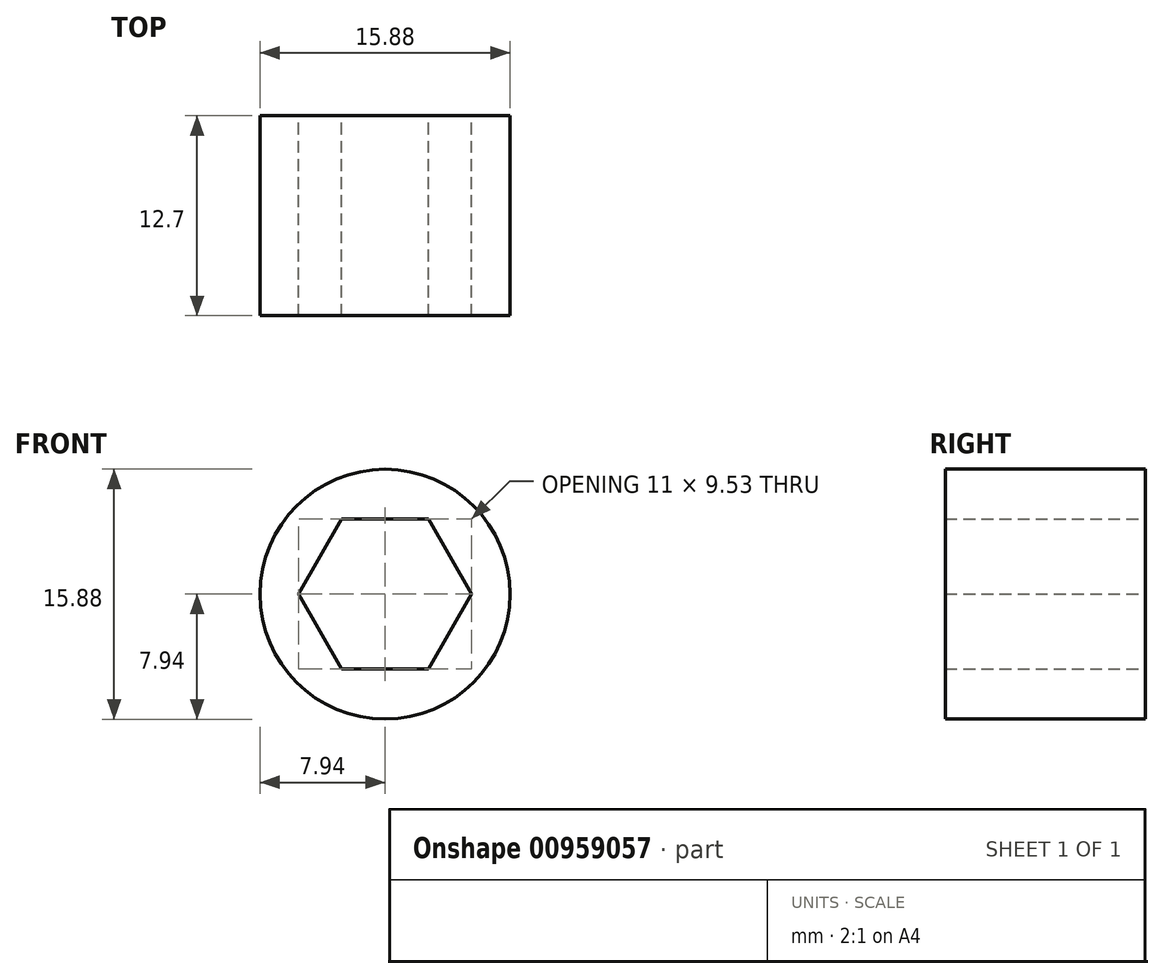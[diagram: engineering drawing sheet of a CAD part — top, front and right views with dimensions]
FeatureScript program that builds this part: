
annotation { "Feature Type Name" : "Feature", "Feature Type Description" : "" }
export const myFeature = defineFeature(function(context is Context, id is Id, definition is map)
    precondition{}
    {
        {
            var Q0;
            Q0=qCreatedBy(makeId("Front.planeOp"),FACE);
            var sketch = newSketch(context, id + "F0", { "sketchPlane" : qUnion([Q0])});
            skCircle(sketch, "E0", {"center": v(0, 0) * mm, "radius": 7.94 * mm});
            skCircle(sketch, "E1.cCircle", {"center": v(0, 0) * mm, "radius": 4.76 * mm, "construction": true});
            skLineSegment(sketch, "E1.0", {"start": v(-2.75, 4.76) * mm, "end": v(2.75, 4.76) * mm});
            skLineSegment(sketch, "E1.1", {"start": v(2.75, 4.76) * mm, "end": v(5.5, 0) * mm});
            skLineSegment(sketch, "E1.2", {"start": v(5.5, 0) * mm, "end": v(2.75, -4.76) * mm});
            skLineSegment(sketch, "E1.3", {"start": v(2.75, -4.76) * mm, "end": v(-2.75, -4.76) * mm});
            skLineSegment(sketch, "E1.4", {"start": v(-2.75, -4.76) * mm, "end": v(-5.5, 0) * mm});
            skLineSegment(sketch, "E1.5", {"start": v(-5.5, 0) * mm, "end": v(-2.75, 4.76) * mm});
            skPoint(sketch, "E1.0.midPoint", {"position": v(0, 4.76) * mm});
            skSolve(sketch);
        }
        {
            var Q0;
            Q0 = qSketchRegion(id + "F0", true);
            extrude(context, id + "F1", {"entities" : qUnion([Q0]), "depth" : 12.7 * mm, "offsetDistance" : 25.4 * mm});
        }
    });
